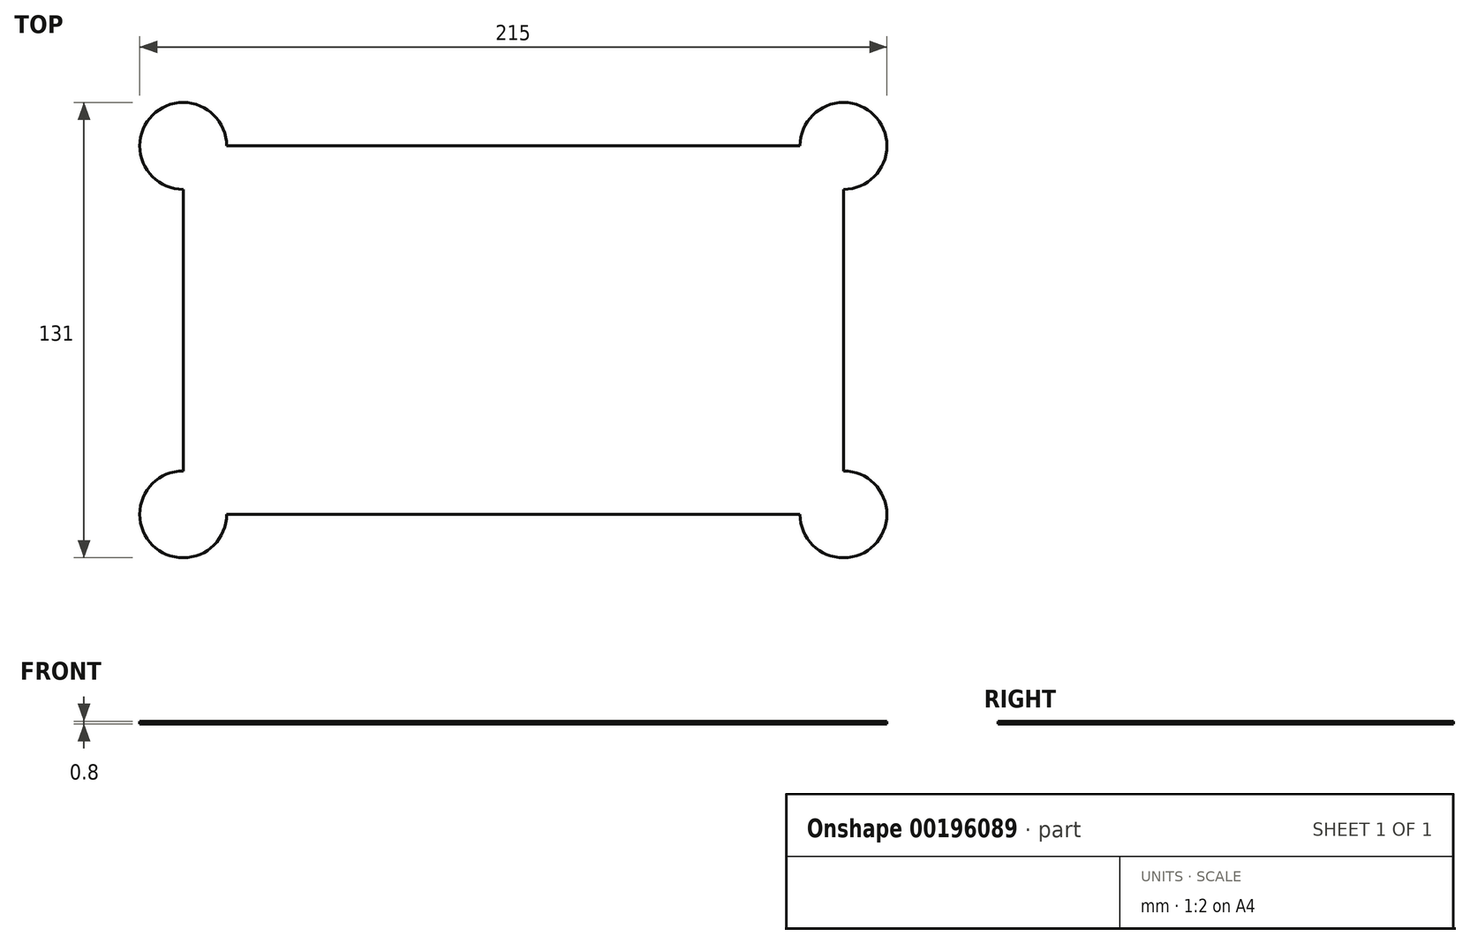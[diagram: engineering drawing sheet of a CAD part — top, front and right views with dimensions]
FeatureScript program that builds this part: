
annotation { "Feature Type Name" : "Feature", "Feature Type Description" : "" }
export const myFeature = defineFeature(function(context is Context, id is Id, definition is map)
    precondition{}
    {
        {
            var Q0;
            Q0=qCreatedBy(makeId("Top.planeOp"),FACE);
            var sketch = newSketch(context, id + "F0", { "sketchPlane" : qUnion([Q0])});
            skLineSegment(sketch, "E0.bottom", {"start": v(0, 0) * mm, "end": v(-190, 0) * mm});
            skLineSegment(sketch, "E0.top", {"start": v(0, 106) * mm, "end": v(-190, 106) * mm});
            skLineSegment(sketch, "E0.left", {"start": v(0, 0) * mm, "end": v(0, 106) * mm});
            skLineSegment(sketch, "E0.right", {"start": v(-190, 0) * mm, "end": v(-190, 106) * mm});
            skSolve(sketch);
        }
        {
            var Q0;
            Q0=makeQuery(id+"F0.imprint","IMPRINT",FACE,{"disambiguationData":[TD([[makeQuery(id+"F0.imprint","IMPRINT",EDGE,{"derivedFrom":sQuery(id+"F0.wireOp",EDGE,"2yAqHf39-Fc5o-gFfP-nSkp-kWoTTWPsp9CE.bottom")}),-1.0]])]});
            var Q1;
            Q1=makeQuery(id+"F0.imprint","IMPRINT",FACE,{"disambiguationData":[TD([[makeQuery(id+"F0.imprint","IMPRINT",EDGE,{"derivedFrom":sQuery(id+"F0.wireOp",EDGE,"E0.bottom")}),-1.0]])]});
            extrude(context, id + "F1", {"entities" : qUnion([Q0, Q1]), "depth" : 0.8 * mm});
        }
        {
            var Q0;
            Q0=makeQuery(id+"F1.opExtrude","CAP_FACE",FACE,{"disambiguationData":[OSD([sQuery(id+"F0.wireOp",EDGE,"E0.bottom"),sQuery(id+"F0.wireOp",EDGE,"E0.top"),sQuery(id+"F0.wireOp",EDGE,"E0.left"),sQuery(id+"F0.wireOp",EDGE,"E0.right"),sQuery(id+"F0.wireOp",EDGE,"2yAqHf39-Fc5o-gFfP-nSkp-kWoTTWPsp9CE.top"),sQuery(id+"F0.wireOp",EDGE,"2yAqHf39-Fc5o-gFfP-nSkp-kWoTTWPsp9CE.left"),sQuery(id+"F0.wireOp",EDGE,"2yAqHf39-Fc5o-gFfP-nSkp-kWoTTWPsp9CE.right")])],"isStart":true});
            var sketch = newSketch(context, id + "F2", { "sketchPlane" : qUnion([Q0])});
            skCircle(sketch, "E1", {"center": v(0, 0) * mm, "radius": 12.5 * mm});
            skCircle(sketch, "E2", {"center": v(-190, 0) * mm, "radius": 12.5 * mm});
            skCircle(sketch, "E3", {"center": v(-190, -106) * mm, "radius": 12.5 * mm});
            skCircle(sketch, "E4", {"center": v(0, -106) * mm, "radius": 12.5 * mm});
            skSolve(sketch);
        }
        {
            var Q0;
            Q0 = qSketchRegion(id + "F2", true);
            extrude(context, id + "F3", {"entities" : qUnion([Q0]), "operationType" : NewBodyOperationType.ADD, "oppositeDirection" : true, "depth" : 0.8 * mm});
        }
    });
